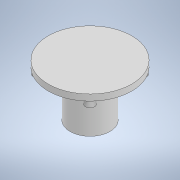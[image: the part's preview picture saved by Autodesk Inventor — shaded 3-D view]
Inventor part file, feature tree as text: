
AUTODESK INVENTOR PART (.ipt)
format: ipt  version: 2021 (Build 250183000, 183)  size: 131,584 bytes
history: native  units: mm
features: extrude x4, sketch x4, other x1
ambient origin geometry x8: Origin, YZ Plane, XZ Plane, XY Plane, X Axis, Y Axis, Z Axis, Center Point
bodies: Body1 (feature_tree)
feature tree (9):
  other  "Sólido1"
  extrude  "Extrusión1"  Depth=17.0mm
  extrude  "Extrusión2"  Depth=3.0mm
  extrude  "Extrusión3"  Depth=3.0mm
  extrude  "Extrusión4"  Depth=4.0mm TaperAngle=0.0deg
  sketch  "Boceto1"  dims[d0=17.0mm d1=17.0mm]
  sketch  "Boceto2"  dims[d2=3.0mm d3=3.0mm]
  sketch  "Boceto3"  dims[d4=3.0mm d5=3.0mm]
  sketch  "Boceto4"  dims[d6=2.0mm d7=0.0mm d8=4.0mm d9=0.0mm d10=13.0mm d11=15.0mm d12=0.0mm d13=10.0mm d14=0.0mm]
